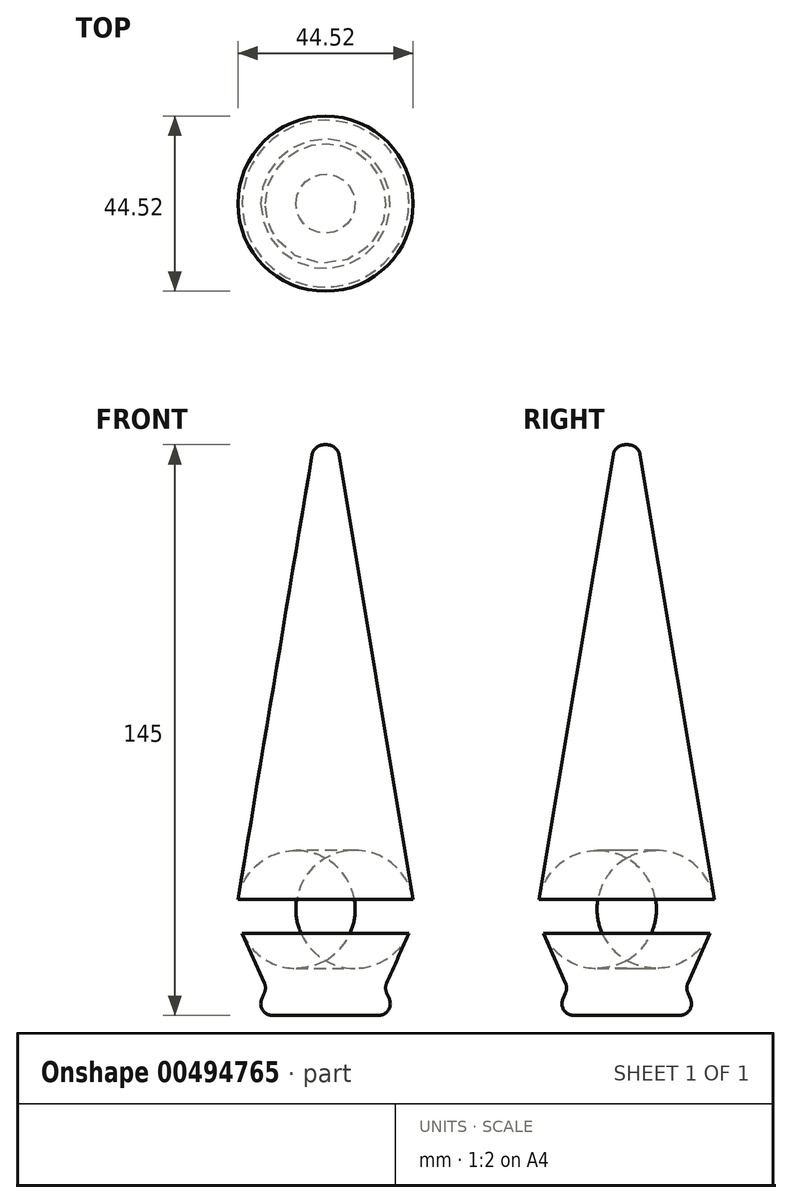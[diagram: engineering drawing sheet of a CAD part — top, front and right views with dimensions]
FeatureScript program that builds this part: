
annotation { "Feature Type Name" : "Feature", "Feature Type Description" : "" }
export const myFeature = defineFeature(function(context is Context, id is Id, definition is map)
    precondition{}
    {
        {
            var Q0;
            Q0=qCreatedBy(makeId("Front.planeOp"),FACE);
            var sketch = newSketch(context, id + "F0", { "sketchPlane" : qUnion([Q0])});
            skLineSegment(sketch, "E0", {"start": v(23, 0) * mm, "end": v(3, 120) * mm});
            skLineSegment(sketch, "E1", {"start": v(0, 120) * mm, "end": v(0, -25) * mm});
            skLineSegment(sketch, "E2", {"start": v(0, -27) * mm, "end": v(0, -53.61) * mm});
            skLineSegment(sketch, "E3", {"start": v(0, 120) * mm, "end": v(3, 120) * mm});
            skLineSegment(sketch, "E4", {"start": v(0, 123.57) * mm, "end": v(0, 137.09) * mm});
            skLineSegment(sketch, "E5", {"start": v(0, -25) * mm, "end": v(18, -25) * mm});
            skLineSegment(sketch, "E6", {"start": v(15, -18) * mm, "end": v(18, -25) * mm});
            skLineSegment(sketch, "E7", {"start": v(23, 0) * mm, "end": v(15, -18) * mm});
            skSolve(sketch);
        }
        {
            var Q0;
            Q0=makeQuery(id+"F0.imprint","IMPRINT",FACE,{"disambiguationData":[TD([[makeQuery(id+"F0.imprint","IMPRINT",EDGE,{"derivedFrom":sQuery(id+"F0.wireOp",EDGE,"E0")}),1.0]])]});
            var Q1;
            Q1=sQuery(id+"F0.wireOp",EDGE,"E4");
            revolve(context, id + "F1", {"entities" : qUnion([Q0]), "axis" : qUnion([Q1]), "revolveType" : RevolveType.ONE_DIRECTION, "angle" : 180 * degree});
        }
        {
            var Q0;
            Q0=makeQuery(id+"F1.opRevolve","SWEPT_BODY",BODY,{"disambiguationData":[OSD([sQuery(id+"F0.wireOp",EDGE,"E0"),sQuery(id+"F0.wireOp",EDGE,"E1"),sQuery(id+"F0.wireOp",EDGE,"E3"),sQuery(id+"F0.wireOp",EDGE,"E5"),sQuery(id+"F0.wireOp",EDGE,"E6"),sQuery(id+"F0.wireOp",EDGE,"7rPBSgOz-U2yj-cz9y-w9HN-AUau6IC02yR6"),sQuery(id+"F0.wireOp",EDGE,"7t8U0qsF-pLgd-GgIO-Hkkh-cJwSIB7hQWLG")])]});
            var Q1;
            Q1=qCreatedBy(makeId("Front.planeOp"),FACE);
            mirror(context, id + "F2", {"operationType" : NewBodyOperationType.ADD, "entities" : qUnion([Q0]), "mirrorPlane" : qUnion([Q1])});
        }
        {
            var Q0;
            {var subQ0=makeQuery(id+"F1.opRevolve","SWEPT_EDGE",EDGE,{"disambiguationData":[OSD([sQuery(id+"F0.wireOp",EDGE,"E0"),sQuery(id+"F0.wireOp",EDGE,"E3")])]});Q0=makeQuery(id+"F2.boolean.opBoolean","MERGE",EDGE,{"derivedFrom":[subQ0,makeQuery(id+"F2.opPattern","COPY",EDGE,{"derivedFrom":subQ0,"instanceName":"1"})]});}
            fillet(context, id + "F3", {"entities" : qUnion([Q0]), "radius" : 3 * mm, "tangentPropagation" : true, "allowEdgeOverflow" : false});
        }
        {
            var Q0;
            {var subQ0=makeQuery(id+"F1.opRevolve","SWEPT_EDGE",EDGE,{"disambiguationData":[OSD([sQuery(id+"F0.wireOp",EDGE,"E6"),sQuery(id+"F0.wireOp",EDGE,"7t8U0qsF-pLgd-GgIO-Hkkh-cJwSIB7hQWLG")])]});Q0=makeQuery(id+"F2.boolean.opBoolean","MERGE",EDGE,{"derivedFrom":[subQ0,makeQuery(id+"F2.opPattern","COPY",EDGE,{"derivedFrom":subQ0,"instanceName":"1"})]});}
            fillet(context, id + "F4", {"entities" : qUnion([Q0]), "radius" : 3 * mm, "tangentPropagation" : true, "allowEdgeOverflow" : false});
        }
        {
            var Q0;
            {var subQ0=makeQuery(id+"F1.opRevolve","SWEPT_EDGE",EDGE,{"disambiguationData":[OSD([sQuery(id+"F0.wireOp",EDGE,"E0"),sQuery(id+"F0.wireOp",EDGE,"E7")])]});Q0=makeQuery(id+"F2.boolean.opBoolean","MERGE",EDGE,{"derivedFrom":[subQ0,makeQuery(id+"F2.opPattern","COPY",EDGE,{"derivedFrom":subQ0,"instanceName":"1"})]});}
            fillet(context, id + "F5", {"entities" : qUnion([Q0]), "radius" : 15 * mm, "tangentPropagation" : true, "allowEdgeOverflow" : false});
        }
    });
